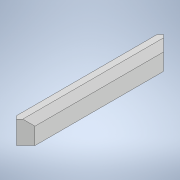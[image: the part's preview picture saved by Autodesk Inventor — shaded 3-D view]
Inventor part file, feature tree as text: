
AUTODESK INVENTOR PART (.ipt)
format: ipt  version: 2021 (Build 250183000, 183)  size: 150,528 bytes
history: native  units: in
note: dims shown in document units (in); Inventor stores cm internally (conversion verified against a paired STEP export)
features: extrude x4, sketch x4, projected_geometry x1
ambient origin geometry x8: Origin, YZ Plane, XZ Plane, XY Plane, X Axis, Y Axis, Z Axis, Center Point
bodies: Solid1 (feature_tree)
feature tree (9):
  extrude  "Extrusion1"  Depth=0.0787in
  extrude  "Extrusion2"  Depth=2.5984in TaperAngle=0.0deg
  extrude  "Extrusion4"  Depth=0.5906in TaperAngle=0.0deg
  extrude  "Extrusion5"  Depth=0.2362in
  sketch  "Sketch1"  dims[d2=0.4331in d4=0.0787in]
  sketch  "Sketch2"  dims[d5=0.3937in d7=2.5984in d8=0.0in]
  sketch  "Sketch5"  dims[d9=0.5906in d10=0.0in d14=0.5906in d15=0.0in]
  projected_geometry  "Projected Loop2"
  sketch  "Sketch6"  dims[d16=0.2362in d17=0.0787in d18=0.2362in d19=1.4719in d20=0.0in]
